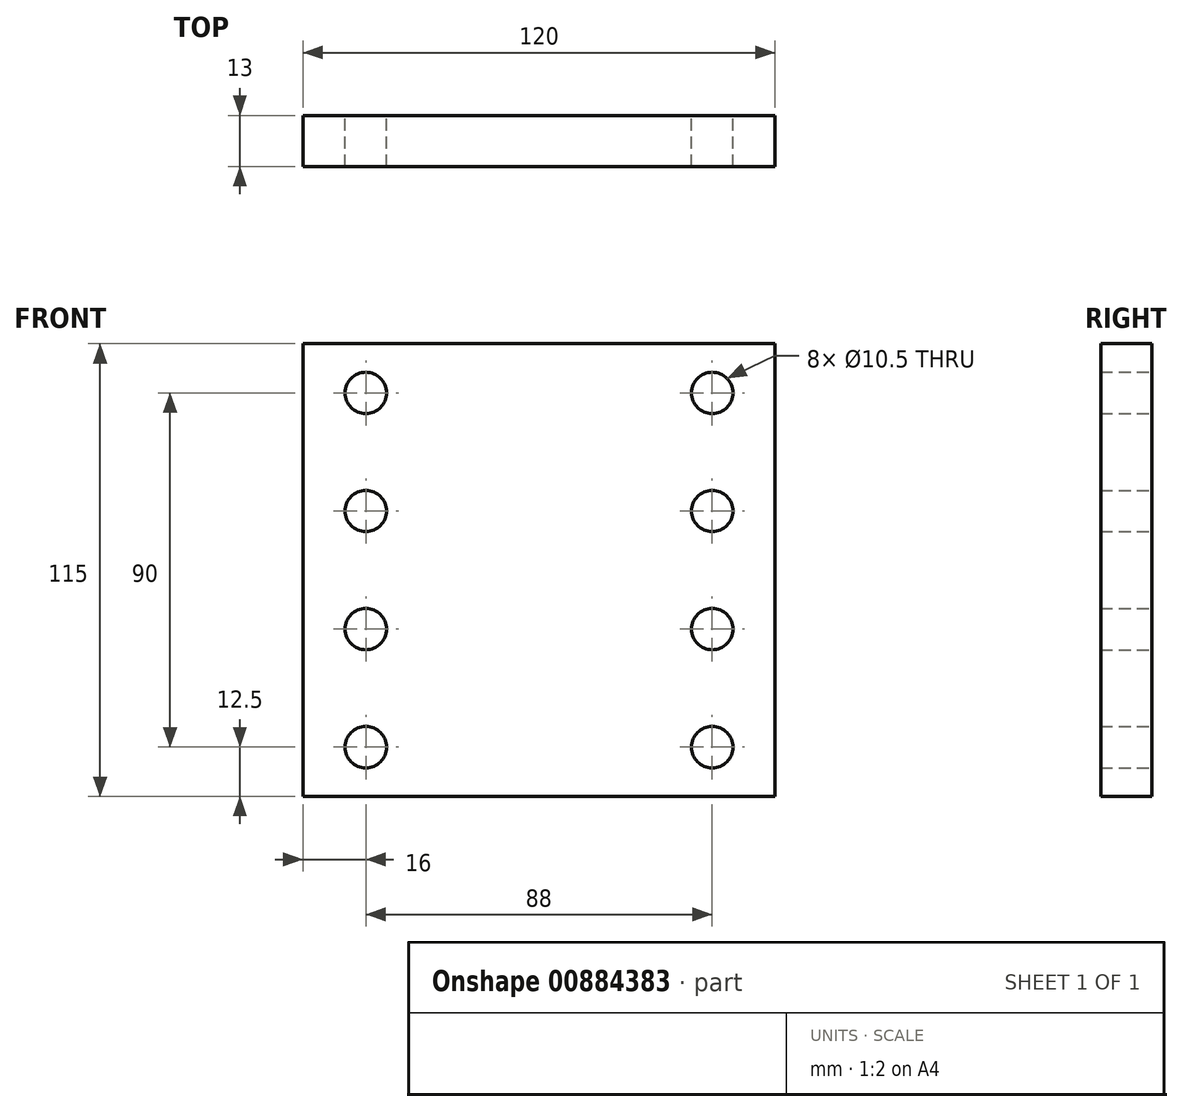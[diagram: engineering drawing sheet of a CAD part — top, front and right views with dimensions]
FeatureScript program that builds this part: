
annotation { "Feature Type Name" : "Feature", "Feature Type Description" : "" }
export const myFeature = defineFeature(function(context is Context, id is Id, definition is map)
    precondition{}
    {
        {
            var Q0;
            Q0=qCreatedBy(makeId("Front.planeOp"),FACE);
            var sketch = newSketch(context, id + "F0", { "sketchPlane" : qUnion([Q0])});
            skLineSegment(sketch, "E0.bottom", {"start": v(60, -57.5) * mm, "end": v(-60, -57.5) * mm});
            skLineSegment(sketch, "E0.top", {"start": v(60, 57.5) * mm, "end": v(-60, 57.5) * mm});
            skLineSegment(sketch, "E0.left", {"start": v(60, -57.5) * mm, "end": v(60, 57.5) * mm});
            skLineSegment(sketch, "E0.right", {"start": v(-60, -57.5) * mm, "end": v(-60, 57.5) * mm});
            skPoint(sketch, "E0.middle", {"position": v(0, 0) * mm});
            skLineSegment(sketch, "E1.bottom", {"start": v(44, -45) * mm, "end": v(-44, -45) * mm});
            skLineSegment(sketch, "E1.top", {"start": v(44, 45) * mm, "end": v(-44, 45) * mm});
            skLineSegment(sketch, "E1.left", {"start": v(44, -45) * mm, "end": v(44, 45) * mm});
            skLineSegment(sketch, "E1.right", {"start": v(-44, -45) * mm, "end": v(-44, 45) * mm});
            skCircle(sketch, "E2", {"center": v(44, 45) * mm, "radius": 5.25 * mm});
            skCircle(sketch, "E3", {"center": v(44, -45) * mm, "radius": 5.25 * mm});
            skCircle(sketch, "E4", {"center": v(44, 15) * mm, "radius": 5.25 * mm});
            skCircle(sketch, "E5", {"center": v(44, -15) * mm, "radius": 5.25 * mm});
            skCircle(sketch, "E6", {"center": v(-44, 45) * mm, "radius": 5.25 * mm});
            skCircle(sketch, "E7", {"center": v(-44, 15) * mm, "radius": 5.25 * mm});
            skCircle(sketch, "E8", {"center": v(-44, -15) * mm, "radius": 5.25 * mm});
            skCircle(sketch, "E9", {"center": v(-44, -45) * mm, "radius": 5.25 * mm});
            skSolve(sketch);
        }
        {
            var Q0;
            Q0=makeQuery(id+"F0.imprint","IMPRINT",FACE,{"disambiguationData":[TD([[makeQuery(id+"F0.imprint","IMPRINT",EDGE,{"derivedFrom":sQuery(id+"F0.wireOp",EDGE,"E0.bottom")}),-1.0]])]});
            var Q1;
            {var subQ8=sQuery(id+"F0.wireOp",EDGE,"E3");var subQ9=sQuery(id+"F0.wireOp",EDGE,"E1.bottom");var subQ10=makeQuery(id+"F0.imprint","INTERSECT",VERTEX,{"derivedFrom":[subQ9,subQ8]});Q1=makeQuery(id+"F0.imprint","IMPRINT",FACE,{"disambiguationData":[TD([[makeQuery(id+"F0.imprint","IMPRINT",EDGE,{"disambiguationData":[TD([[subQ10,-1.0]])],"derivedFrom":subQ9}),-1.0]])]});}
            extrude(context, id + "F1", {"entities" : qUnion([Q0, Q1]), "depth" : 13 * mm, "offsetDistance" : 25 * mm});
        }
    });
